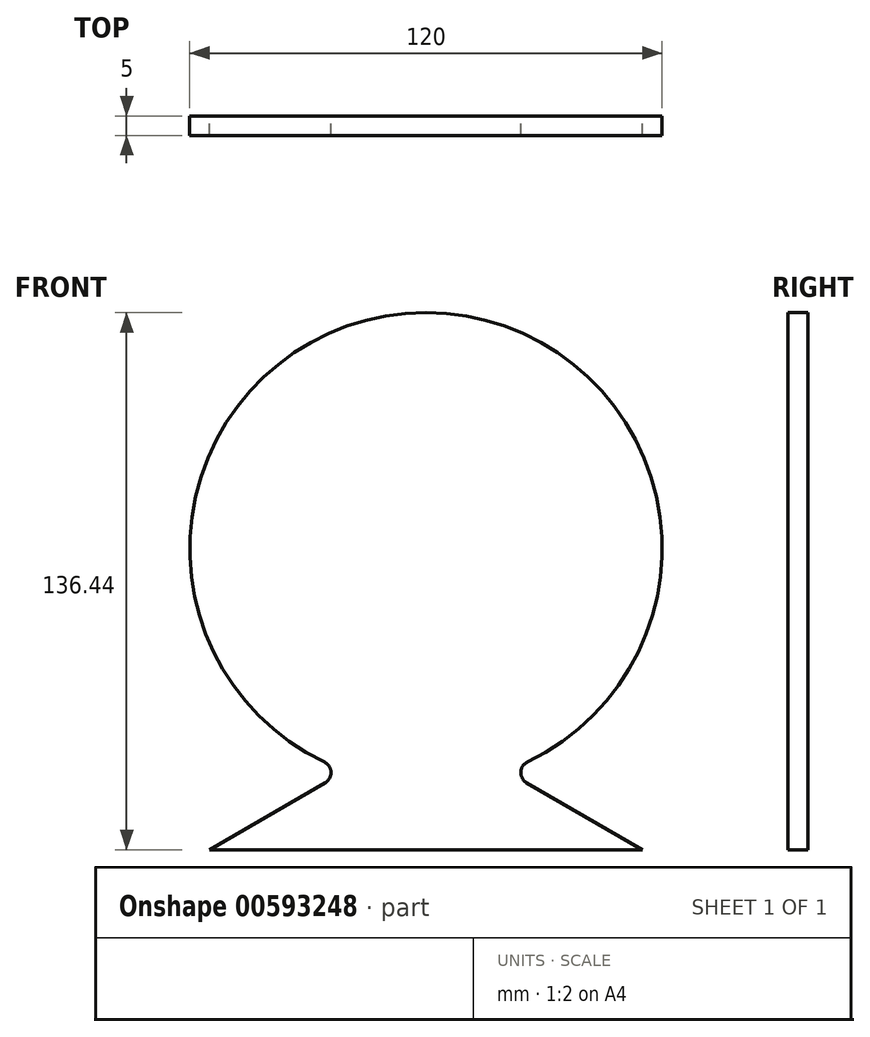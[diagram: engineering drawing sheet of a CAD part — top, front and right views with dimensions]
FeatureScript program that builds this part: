
annotation { "Feature Type Name" : "Feature", "Feature Type Description" : "" }
export const myFeature = defineFeature(function(context is Context, id is Id, definition is map)
    precondition{}
    {
        {
            var Q0;
            Q0=qCreatedBy(makeId("Front.planeOp"),FACE);
            var sketch = newSketch(context, id + "F0", { "sketchPlane" : qUnion([Q0])});
            skLineSegment(sketch, "E0", {"start": v(-27.5, -34.59) * mm, "end": v(82.5, -34.59) * mm});
            skLineSegment(sketch, "E1", {"start": v(-27.5, -34.59) * mm, "end": v(1.9, -17.62) * mm});
            skLineSegment(sketch, "E2", {"start": v(82.5, -34.59) * mm, "end": v(53.1, -17.62) * mm});
            skArc(sketch, "E3", {"start": v(53.31, -12.3) * mm, "mid": v(27.5, 101.85) * mm, "end": v(1.69, -12.3) * mm});
            skPoint(sketch, "E4.visualSharp", {"position": v(7.14, -14.59) * mm});
            skArc(sketch, "E4.filletArc", {"start": v(1.9, -17.62) * mm, "mid": v(3.4, -14.9) * mm, "end": v(1.69, -12.3) * mm});
            skPoint(sketch, "E5.visualSharp", {"position": v(47.86, -14.59) * mm});
            skArc(sketch, "E5.filletArc", {"start": v(53.31, -12.3) * mm, "mid": v(51.6, -14.9) * mm, "end": v(53.1, -17.62) * mm});
            skSolve(sketch);
        }
        {
            var Q0;
            Q0 = qSketchRegion(id + "F0", true);
            extrude(context, id + "F1", {"entities" : qUnion([Q0]), "depth" : 5 * mm, "offsetDistance" : 25 * mm});
        }
    });
